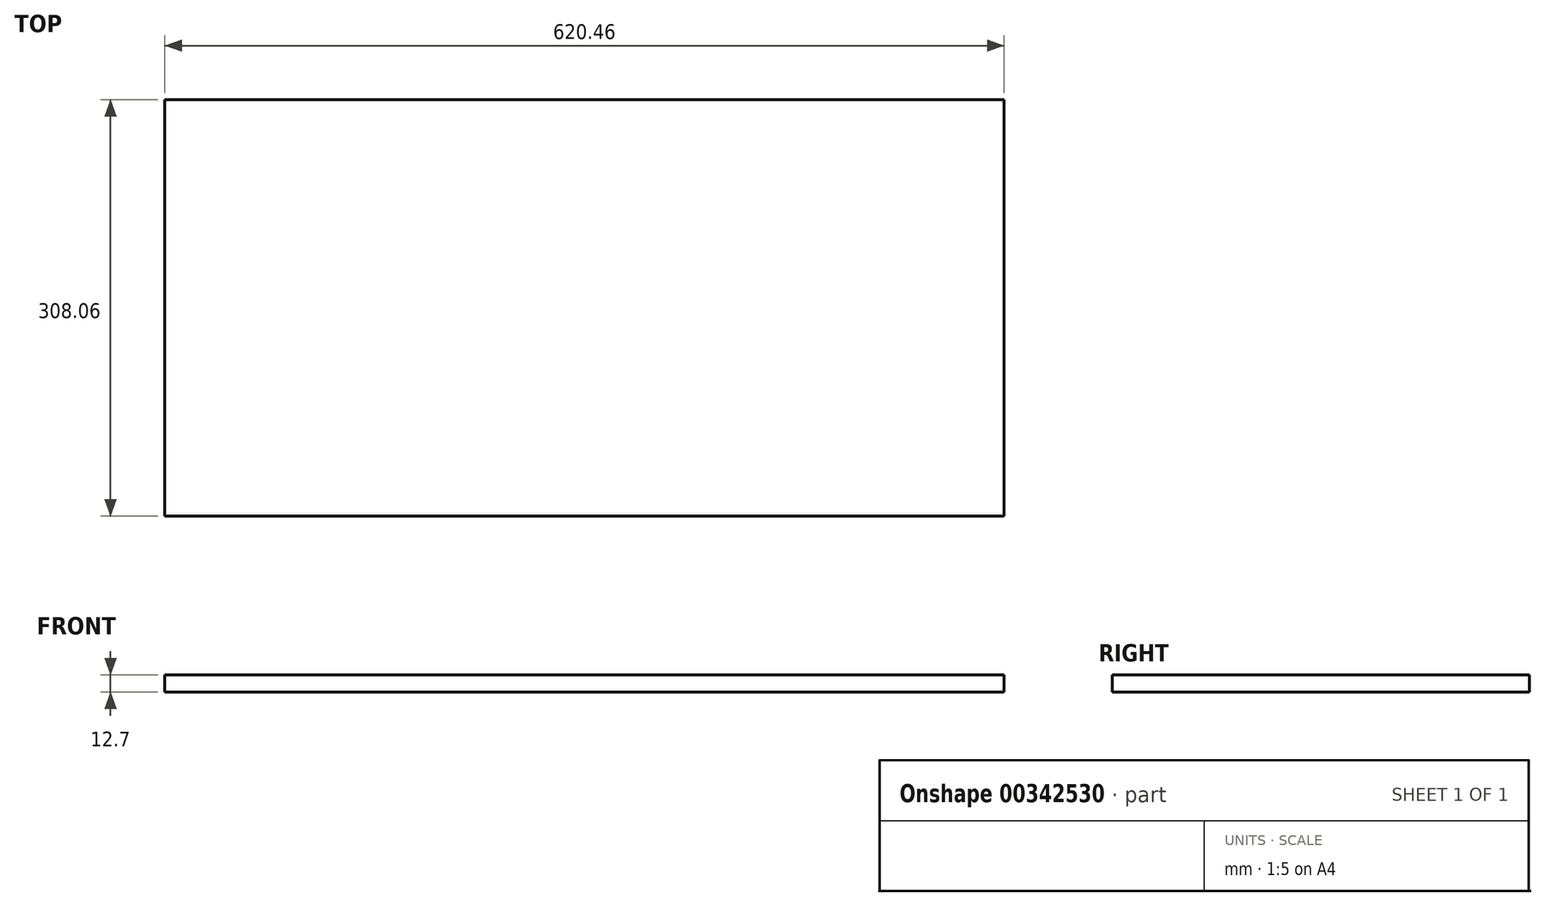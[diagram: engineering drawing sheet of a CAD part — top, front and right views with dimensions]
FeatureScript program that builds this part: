
annotation { "Feature Type Name" : "Feature", "Feature Type Description" : "" }
export const myFeature = defineFeature(function(context is Context, id is Id, definition is map)
    precondition{}
    {
        {
            var Q0;
            Q0=qCreatedBy(makeId("Top.planeOp"),FACE);
            var sketch = newSketch(context, id + "F0", { "sketchPlane" : qUnion([Q0])});
            skLineSegment(sketch, "E0.bottom", {"start": v(310.23, -154.03) * mm, "end": v(-310.23, -154.03) * mm});
            skLineSegment(sketch, "E0.top", {"start": v(310.23, 154.03) * mm, "end": v(-310.23, 154.03) * mm});
            skLineSegment(sketch, "E0.left", {"start": v(310.23, -154.03) * mm, "end": v(310.23, 154.03) * mm});
            skLineSegment(sketch, "E0.right", {"start": v(-310.23, -154.03) * mm, "end": v(-310.23, 154.03) * mm});
            skPoint(sketch, "E0.middle", {"position": v(0, 0) * mm});
            skSolve(sketch);
        }
        {
            var Q0;
            Q0=makeQuery(id+"F0.imprint","IMPRINT",FACE,{"disambiguationData":[TD([[makeQuery(id+"F0.imprint","IMPRINT",EDGE,{"derivedFrom":sQuery(id+"F0.wireOp",EDGE,"E0.bottom")}),-1.0]])]});
            extrude(context, id + "F1", {"entities" : qUnion([Q0]), "depth" : 12.7 * mm});
        }
    });
